# Revit family: CH-WA25
name_source: partatom
category: Lighting Fixtures
revit_build: Autodesk Revit Architecture 2012 (Build: 20110309_2315(x64)
units: mm (PartAtom-declared; Revit-internal decimal feet)

## types (2) — shared parameters
Color Filter = 16777215
Colour = Black
Default Elevation = 48"
Description = For 20 to 30 foot mounting heights in areas that call for three dimensional illumination as well as good looks.
Dimming Lamp Color Temperature Shift = <None>
Emit from Line Length = 12"
Finish = Aluminium
Glass = Glass
Lamp = 1
Light source = 0 lx
Manufacturer = Hubbell Industrial lighting
Manufacturer Fax = (864)-678-1065
Model = CH WA 25
Product Documentation Link = http://www.hubbellindustrial.com
Product Page URL = http://www.hubbellindustrial.com
Tilt Angle = 180.00°
URL = http://www.hubbellindustrial.com
Wattage Comments = 100W/100W

## per-type parameters (varying)
| type | Photometric Web File |
| CH10Hxx-WA25 LU/LP: 1@104500 SC @2/@4: 1.7/1.5 | HP07531.IES |
| CH1xHxx-WA25-QSS LU/LP: 1@5000 SC @2/@4: 2.2/1.8/1hp09678.ies | hp09678.ies |

## geometry (parser evidence)
native form markers: Blend x4, Sweep x1
no freeform markers — native parametric forms only
